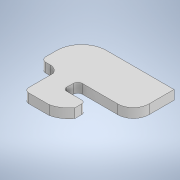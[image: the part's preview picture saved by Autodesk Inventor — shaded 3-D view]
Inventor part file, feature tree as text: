
AUTODESK INVENTOR PART (.ipt)
format: ipt  version: 2022 (Build 260153000, 153)  size: 146,432 bytes
history: native  units: mm
features: extrude x1, sketch x1
ambient origin geometry x8: Origin, YZ Plane, XZ Plane, XY Plane, X Axis, Y Axis, Z Axis, Center Point
bodies: Solid1 (feature_tree)
feature tree (2):
  extrude  "Extrusion1"  Depth=29.6mm
  sketch  "Sketch1"  dims[d0=24.2mm d1=29.6mm d2=11.2mm d3=5.8mm d4=13.0mm d5=6.5mm d6=6.0mm d7=16.0mm d8=8.0mm d9=8.0mm d10=10.0mm d11=5.0mm d12=5.0mm d13=3.0mm d14=2.2mm d15=1.5mm d16=1.5mm d17=1.1mm d18=1.1mm d19=6.0mm d20=3.0mm d21=3.0mm d22=3.0mm d23=1.5mm d24=1.5mm d25=2.0mm d26=1.0mm d27=1.0mm d28=5.0mm d29=3.25mm d30=3.0mm d31=0.0mm d32=3.0mm d33=1.5mm d34=1.5mm]
